# Revit family: PX-A-G-HT
name_source: partatom
category: Lighting Fixtures
units: mm (PartAtom-declared; Revit-internal decimal feet)

## family parameters
Cut with Voids When Loaded = No
Host = Face
Light Source = No
Maintain Annotation Orientation = No
Part Type = Normal
Room Calculation Point = No
Round Connector Dimension = Use Diameter
Shared = No

## types (2) — shared parameters
Default Elevation = 4' - 0"
Description = The Paco Aqua Exit (PX-A) is the newest edition to our Paco series. It
has dual input 120/277V and is offered as AC only and self-powered. The 
Paco Aqua Exit self powered version uses a rechargeable, maintenance 
free 3.6V 900mAH nickel cadmium battery. The circuit board features 
an onboard solid state transformer, low voltage disconnect and 
brownout protection. Available in either red or green LEDs consuming 
less than 2W
HOUSING MATERIAL = HOUSING MATERIAL
LENS MATERIAL = LENS MATERIAL
Lamp = LED
Manufacturer = BEGHELLI
Model = PX-A-G-HT
Type Comments = EM SIGN
Type Image = PACO AQUA.PNG
Wattage Comments = 2W

## per-type parameters (varying)
| type | LETTERS |
| PX-A-G-HT | LETTER MATERIAL GREEN |
| PX-A-R-HT | LETTER MATERIAL RED |

## geometry (parser evidence)
native form markers: Sweep x28
no freeform markers — native parametric forms only
